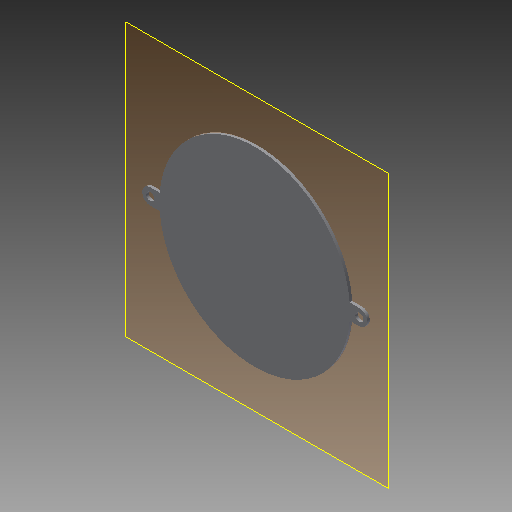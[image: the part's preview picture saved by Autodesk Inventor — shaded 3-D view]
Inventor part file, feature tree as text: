
AUTODESK INVENTOR PART (.ipt)
format: ipt  version: 2017 (Build 210142000, 142)  size: 95,232 bytes
history: native  units: mm
features: plane x1, extrude x1, sketch x1
ambient origin geometry x8: Origin, YZ Plane, XZ Plane, XY Plane, X Axis, Y Axis, Z Axis, Center Point
bodies: Body1 (feature_tree)
feature tree (3):
  plane  "Work Plane1"
  extrude  "Extrusion3"  Depth=36.0mm
  sketch  "Sketch1"  dims[d0=36.0mm d19=36.0mm d26=1.0mm d27=0.0mm]
